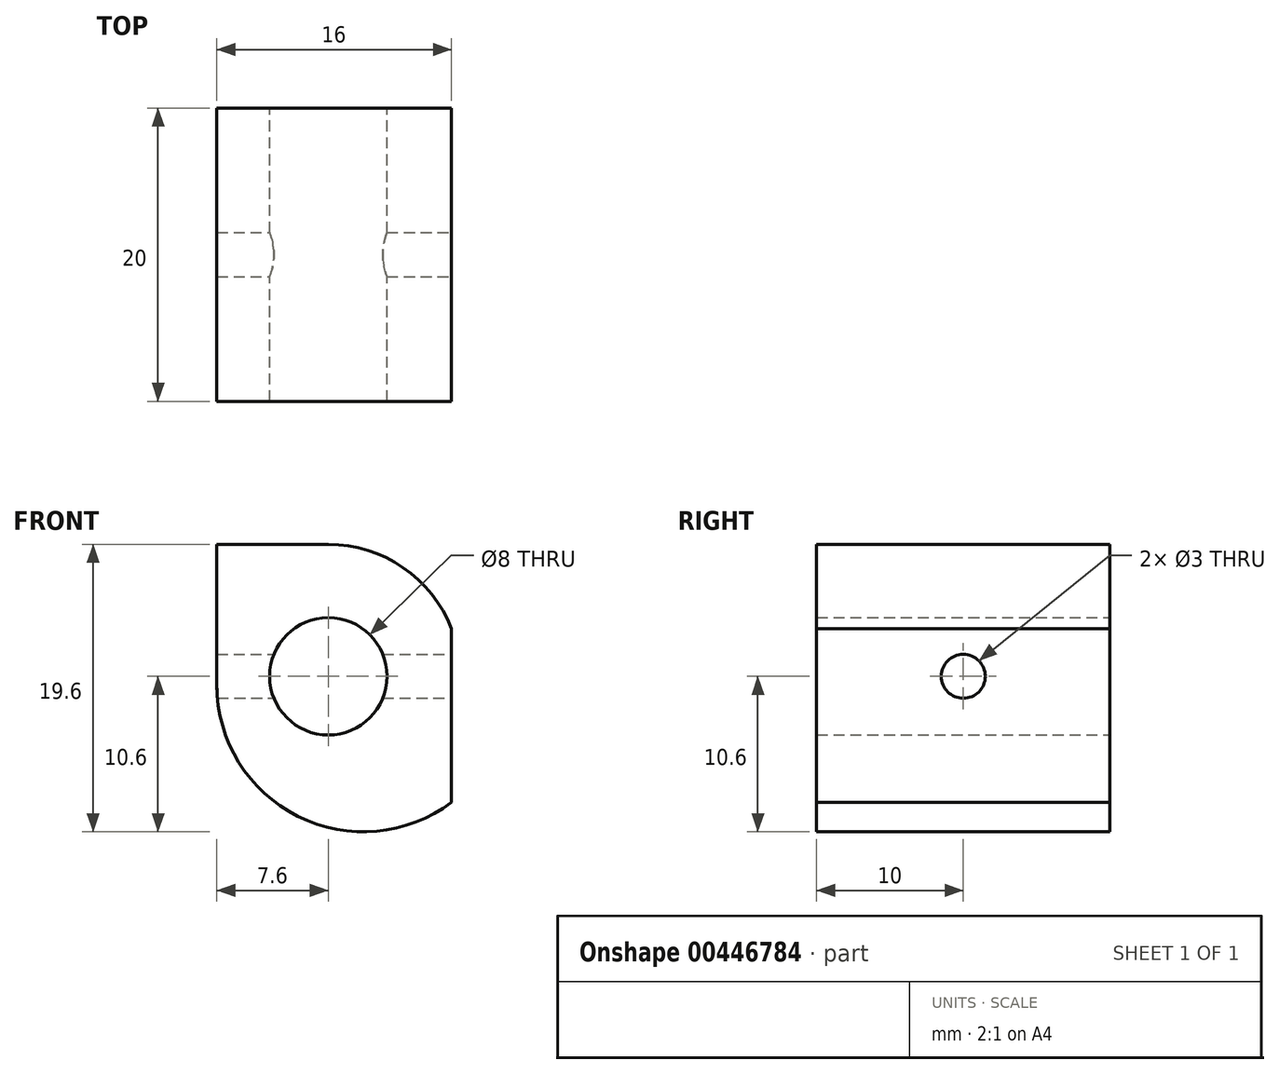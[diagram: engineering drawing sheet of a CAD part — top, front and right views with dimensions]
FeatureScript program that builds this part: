
annotation { "Feature Type Name" : "Feature", "Feature Type Description" : "" }
export const myFeature = defineFeature(function(context is Context, id is Id, definition is map)
    precondition{}
    {
        {
            var Q0;
            Q0=qCreatedBy(makeId("Front.planeOp"),FACE);
            var sketch = newSketch(context, id + "F0", { "sketchPlane" : qUnion([Q0])});
            skCircle(sketch, "E0", {"center": v(0, 0) * mm, "radius": 4 * mm});
            skLineSegment(sketch, "E1", {"start": v(8.4, -8.6) * mm, "end": v(8.4, 3.23) * mm});
            skLineSegment(sketch, "E2", {"start": v(0, 9) * mm, "end": v(-7.6, 9) * mm});
            skLineSegment(sketch, "E3", {"start": v(-7.6, 9) * mm, "end": v(-7.6, -0.6) * mm});
            skLineSegment(sketch, "E4", {"start": v(0, 0) * mm, "end": v(5.62, 0) * mm, "construction": true});
            skPoint(sketch, "E5.visualSharp", {"position": v(8.4, 9) * mm});
            skArc(sketch, "E6", {"start": v(8.4, 3.23) * mm, "mid": v(5.1, 7.42) * mm, "end": v(0, 9) * mm});
            skLineSegment(sketch, "E7.0", {"start": v(2.4, 9) * mm, "end": v(2.4, -10.6) * mm, "construction": true});
            skLineSegment(sketch, "E8.0", {"start": v(8.4, -0.6) * mm, "end": v(-7.6, -0.6) * mm, "construction": true});
            skArc(sketch, "E9", {"start": v(-7.6, -0.6) * mm, "mid": v(-2.07, -9.54) * mm, "end": v(8.4, -8.6) * mm});
            skSolve(sketch);
        }
        {
            var Q0;
            Q0 = qSketchRegion(id + "F0", true);
            extrude(context, id + "F1", {"entities" : qUnion([Q0]), "depth" : 20 * mm, "symmetric" : true});
        }
        {
            var Q0;
            Q0=makeQuery(id+"F1.opExtrude","SWEPT_FACE",FACE,{"disambiguationData":[OSD([sQuery(id+"F0.wireOp",EDGE,"E1")])]});
            var sketch = newSketch(context, id + "F2", { "sketchPlane" : qUnion([Q0])});
            skCircle(sketch, "E10", {"center": v(0, 0) * mm, "radius": 1.5 * mm});
            skSolve(sketch);
        }
        {
            var Q0;
            Q0 = qSketchRegion(id + "F2", true);
            extrude(context, id + "F3", {"entities" : qUnion([Q0]), "operationType" : NewBodyOperationType.REMOVE, "endBound" : BoundingType.THROUGH_ALL, "oppositeDirection" : true, "depth" : 25 * mm});
        }
    });
